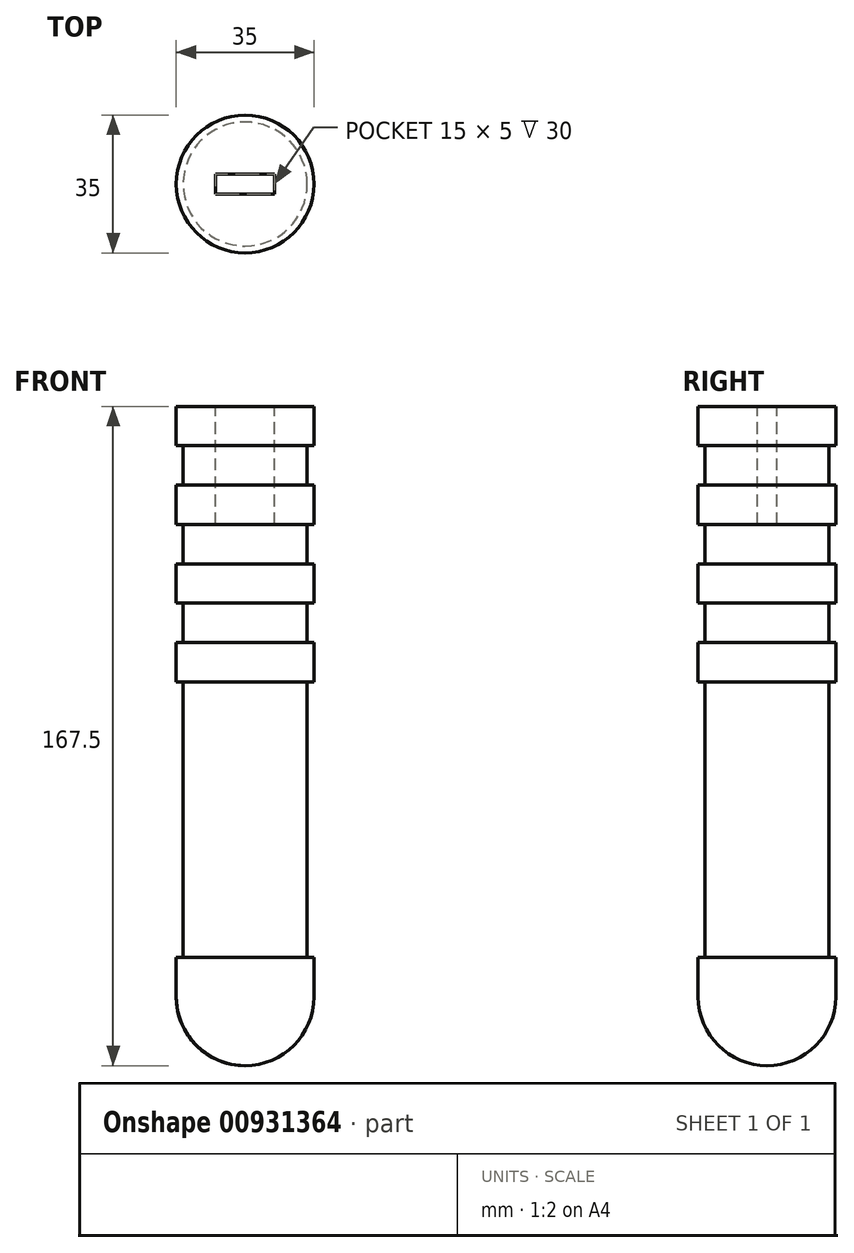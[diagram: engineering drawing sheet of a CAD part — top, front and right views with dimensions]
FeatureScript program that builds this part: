
annotation { "Feature Type Name" : "Feature", "Feature Type Description" : "" }
export const myFeature = defineFeature(function(context is Context, id is Id, definition is map)
    precondition{}
    {
        {
            var Q0;
            Q0=qCreatedBy(makeId("Front.planeOp"),FACE);
            var sketch = newSketch(context, id + "F0", { "sketchPlane" : qUnion([Q0])});
            skArc(sketch, "E0", {"start": v(0, -17.5) * mm, "mid": v(12.37, -12.37) * mm, "end": v(17.5, 0) * mm});
            skLineSegment(sketch, "E1", {"start": v(0, -17.5) * mm, "end": v(0, 150) * mm});
            skLineSegment(sketch, "E2", {"start": v(0, 150) * mm, "end": v(17.5, 150) * mm});
            skLineSegment(sketch, "E3", {"start": v(17.5, 150) * mm, "end": v(17.5, 140) * mm});
            skLineSegment(sketch, "E4", {"start": v(17.5, 140) * mm, "end": v(15.75, 140) * mm});
            skLineSegment(sketch, "E5", {"start": v(15.75, 140) * mm, "end": v(15.75, 130) * mm});
            skLineSegment(sketch, "E6", {"start": v(15.75, 130) * mm, "end": v(17.5, 130) * mm});
            skLineSegment(sketch, "E7", {"start": v(17.5, 130) * mm, "end": v(17.5, 120) * mm});
            skLineSegment(sketch, "E8", {"start": v(17.5, 120) * mm, "end": v(15.75, 120) * mm});
            skLineSegment(sketch, "E9", {"start": v(15.75, 120) * mm, "end": v(15.75, 110) * mm});
            skLineSegment(sketch, "E10", {"start": v(15.75, 110) * mm, "end": v(17.5, 110) * mm});
            skLineSegment(sketch, "E11", {"start": v(17.5, 110) * mm, "end": v(17.5, 100) * mm});
            skLineSegment(sketch, "E12", {"start": v(17.5, 100) * mm, "end": v(15.75, 100) * mm});
            skLineSegment(sketch, "E13", {"start": v(15.75, 100) * mm, "end": v(15.75, 90) * mm});
            skLineSegment(sketch, "E14", {"start": v(15.75, 90) * mm, "end": v(17.5, 90) * mm});
            skLineSegment(sketch, "E15", {"start": v(17.5, 90) * mm, "end": v(17.5, 80) * mm});
            skLineSegment(sketch, "E16", {"start": v(17.5, 80) * mm, "end": v(15.75, 80) * mm});
            skLineSegment(sketch, "E17", {"start": v(15.75, 80) * mm, "end": v(15.75, 10) * mm});
            skLineSegment(sketch, "E18", {"start": v(15.75, 10) * mm, "end": v(17.5, 10) * mm});
            skLineSegment(sketch, "E19", {"start": v(17.5, 0) * mm, "end": v(17.5, 10) * mm});
            skSolve(sketch);
        }
        {
            var Q0;
            Q0 = qSketchRegion(id + "F0", true);
            var Q1;
            Q1=sQuery(id+"F0.wireOp",EDGE,"E1");
            revolve(context, id + "F1", {"surfaceOperationType" : NewSurfaceOperationType.NEW, "entities" : qUnion([Q0]), "axis" : qUnion([Q1]), "revolveType" : RevolveType.FULL});
        }
        {
            var Q0;
            Q0=makeQuery(id+"F1.opRevolve","SWEPT_FACE",FACE,{"disambiguationData":[OSD([sQuery(id+"F0.wireOp",EDGE,"E2")])]});
            var sketch = newSketch(context, id + "F2", { "sketchPlane" : qUnion([Q0])});
            skLineSegment(sketch, "E20.bottom", {"start": v(7.5, -2.5) * mm, "end": v(-7.5, -2.5) * mm});
            skLineSegment(sketch, "E20.top", {"start": v(7.5, 2.5) * mm, "end": v(-7.5, 2.5) * mm});
            skLineSegment(sketch, "E20.left", {"start": v(7.5, -2.5) * mm, "end": v(7.5, 2.5) * mm});
            skLineSegment(sketch, "E20.right", {"start": v(-7.5, -2.5) * mm, "end": v(-7.5, 2.5) * mm});
            skPoint(sketch, "E20.middle", {"position": v(0, 0) * mm});
            skSolve(sketch);
        }
        {
            var Q0;
            Q0 = qSketchRegion(id + "F2", true);
            extrude(context, id + "F3", {"entities" : qUnion([Q0]), "operationType" : NewBodyOperationType.REMOVE, "oppositeDirection" : true, "depth" : 30 * mm, "offsetDistance" : 25 * mm});
        }
    });
